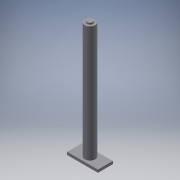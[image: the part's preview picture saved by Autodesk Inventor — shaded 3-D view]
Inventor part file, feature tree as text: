
AUTODESK INVENTOR PART (.ipt)
format: ipt  version: 2016 (Build 200138000, 138)  size: 110,080 bytes
history: native  units: in
note: dims shown in document units (in); Inventor stores cm internally (conversion verified against a paired STEP export)
features: extrude x4, sketch x4
ambient origin geometry x8: Origin, YZ Plane, XZ Plane, XY Plane, X Axis, Y Axis, Z Axis, Center Point
bodies: Solid1 (feature_tree)
feature tree (8):
  extrude  "Extrusion1"  Depth=2.8976in TaperAngle=0.0deg
  extrude  "Extrusion2"  Depth=2.7874in TaperAngle=0.0deg
  extrude  "Extrusion3"  Depth=0.0394in
  extrude  "Extrusion4"  Depth=0.0689in
  sketch  "Sketch1"  dims[d0=0.2579in d1=2.8976in d2=0.0in]
  sketch  "Sketch2"  dims[d3=0.1496in d4=2.7874in d5=0.0in]
  sketch  "Sketch3"  dims[d6=0.0394in d7=0.0in d8=0.186in]
  sketch  "Sketch4"  dims[d9=0.372in d10=0.3839in d11=0.7677in d12=0.0689in d13=0.0in]
